FCSTD DOCUMENT  (FreeCAD 1.0R39109 (Git))
Label: Tail_Hinge_Inner
License: All rights reserved
LicenseURL: http://en.wikipedia.org/wiki/All_rights_reserved
objects: App::Link×3, Spreadsheet::Sheet×1, App::Part×1
EXTERNAL_REF file=Tail_Hinge_Inner_Pipe.FCStd obj=Tube
EXTERNAL_REF file=../../../Master_of_Puppets.FCStd obj=Spreadsheet
EXTERNAL_REF file=../../../Master_of_Puppets.FCStd obj=Tail
EXTERNAL_REF file=../Junction/Tail_Hinge_Junction.FCStd obj=Part
EXTERNAL_REF file=Tail_Hinge_Inner_Pipe_Cover.FCStd obj=Cylinder

FEATURE [App::Link] Link  label="Pipe"
  LinkPlacement = pos=(31.9025,0,-7.21663) rot=(0,1,0;0.349066rad)
  LinkedObject = -> <external Tail_Hinge_Inner_Pipe.FCStd>#Tube
  Placement = pos=(31.9025,0,-7.21663) rot=(0,1,0;0.349066rad)
  expr: .LinkPlacement.Base.x = Spreadsheet.TailHingePipeX
  expr: .LinkPlacement.Base.z = Spreadsheet.TailHingePipeZ
  expr: Placement = Spreadsheet.HingeInnerPipePlacement
FEATURE [Spreadsheet::Sheet] Spreadsheet
  cells = A1='Inputs; A2='VerticalPlaneAngle; B2(VerticalPlaneAngle)==Master_of_Puppets#Spreadsheet.VerticalPlaneAngle; A3='HingeInnerPipeRadius; B3(HingeInnerPipeRadius)==Master_of_Puppets#Tail.HingeInnerPipeRadius; A4='FlatMetalThickness; B4(FlatMetalThickness)==Master_of_Puppets#Spreadsheet.FlatMetalThickness; A5='Height; B5(Height)==Master_of_Puppets#Tail.TailHingeJunctionHeight; A6='Chamfer; B6(Chamfer)==Master_of_Puppets#Tail.TailHingeJunctionChamfer; A7='FullWidth; B7(FullWidth)==Master_of_Puppets#Tail.TailHingeJunctionFullWidth; A8='TailHingePipeZ; B8(TailHingePipeZ)==Master_of_Puppets#Tail.TailHingePipeZ; A9='TailHingePipeX; B9(TailHingePipeX)==Master_of_Puppets#Tail.TailHingePipeX; A10='HingeInnerPipeLength; B10(HingeInnerPipeLength)==Master_of_Puppets#Tail.HingeInnerPipeLength; A11='HingeInnerPipeDisplayCover; B11(HingeInnerPipeDisplayCover)==Master_of_Puppets#Tail.HingeInnerPipeDisplayCover; A12='Calculated; A13='TailHingeJunctionX; B13(TailHingeJunctionX)==-Chamfer; A14='HingeInnerPipePlacement; B14(HingeInnerPipePlacement)==placement(vector(TailHingePipeX; 0; TailHingePipeZ); vector(0; 1; 0); VerticalPlaneAngle); A15='HingeInnerPipeCoverPlacement; B15(HingeInnerPipeCoverPlacement)==HingeInnerPipePlacement * placement(vector(0; 0; HingeInnerPipeLength); vector(0; 0; 1); 0)
FEATURE [App::Link] Link005  label="Junction"
  LinkPlacement = pos=(-12.075,0,0) rot=(0,0,1;0rad)
  LinkedObject = -> <external ../Junction/Tail_Hinge_Junction.FCStd>#Part
  Placement = pos=(-12.075,0,0) rot=(0,0,1;0rad)
  expr: .Placement.Base.x = Spreadsheet.TailHingeJunctionX
FEATURE [App::Link] Link006  label="Tail_Hinge_Inner_Pipe_Cover"
  LinkPlacement = pos=(93.2691,0,161.387) rot=(0,1,0;0.349066rad)
  LinkedObject = -> <external Tail_Hinge_Inner_Pipe_Cover.FCStd>#Cylinder
  Placement = pos=(93.2691,0,161.387) rot=(0,1,0;0.349066rad)
  expr: Placement = Spreadsheet.HingeInnerPipeCoverPlacement
  expr: Visibility = Spreadsheet.HingeInnerPipeDisplayCover
FEATURE [App::Part] Part001  label="Tail_Hinge_Inner"
  Group = -> [Link,Link005,Link006]
  Origin = -> Origin001

RESOLVED EXTERNAL PARTS (link-assembly join: the EXTERNAL_REF files above that resolve inside this repo's crawl, each included once):
---- part ../../../Master_of_Puppets.FCStd = doc fcstd_6404554055c4 (61625 chars; too large to inline — full recipe in that document) ----
---- part ../Junction/Tail_Hinge_Junction.FCStd = doc fcstd_d0f173730f93 ----
FCSTD DOCUMENT  (FreeCAD 0.21R33675 (Git))
Label: Tail_Hinge_Junction
License: All rights reserved
LicenseURL: http://en.wikipedia.org/wiki/All_rights_reserved
objects: App::Link×3, Spreadsheet::Sheet×1, App::Part×1
EXTERNAL_REF file=../../../Master_of_Puppets.FCStd obj=Spreadsheet
EXTERNAL_REF file=../../../Master_of_Puppets.FCStd obj=Tail
EXTERNAL_REF file=Tail_Hinge_Junction_Cover_Top.FCStd obj=PocketBody
EXTERNAL_REF file=Tail_Hinge_Junction_Cover_Side.FCStd obj=PadBody

FEATURE [Spreadsheet::Sheet] Spreadsheet
  cells = A1='Inputs; A2='YawPipeDiameter; B2(YawPipeDiameter)==Master_of_Puppets#Spreadsheet.YawPipeDiameter; A3='HingeInnerPipeRadius; B3(HingeInnerPipeRadius)==Master_of_Puppets#Tail.HingeInnerPipeRadius; A4='FlatMetalThickness; B4(FlatMetalThickness)==Master_of_Puppets#Spreadsheet.FlatMetalThickness; A5='Height; B5(Height)==Master_of_Puppets#Tail.TailHingeJunctionHeight; A6='FullWidth; B6(FullWidth)==Master_of_Puppets#Tail.TailHingeJunctionFullWidth; A7='Calculated; A8='YawPipeRadius; B8(YawPipeRadius)==YawPipeDiameter / 2; A9='SideCoverAngle; B9(SideCoverAngle)==YawPipeRadius == HingeInnerPipeRadius ? 0 deg : 90 deg - atan(FullWidth / (YawPipeRadius - HingeInnerPipeRadius)); A10='TailHingeTopCoverZ; B10(TailHingeTopCoverZ)==Height - FlatMetalThickness; A11='FrontTailHingeSideCoverY; B11(FrontTailHingeSideCoverY)==-YawPipeRadius; A12='BackTailHingeSideCoverY; B12(BackTailHingeSideCoverY)==YawPipeRadius + FlatMetalThickness
FEATURE [App::Link] Link  label="Top_Cover"
  LinkPlacement = pos=(0,0,70) rot=(0,0,1;0rad)
  LinkedObject = -> <external Tail_Hinge_Junction_Cover_Top.FCStd>#PocketBody
  Placement = pos=(0,0,70) rot=(0,0,1;0rad)
  expr: .Placement.Base.z = Spreadsheet.TailHingeTopCoverZ
FEATURE [App::Link] Link001  label="Cover_Side_Front"
  LinkPlacement = pos=(0,-30.15,0) rot=(0,0,1;0rad)
  LinkTransform = true
  LinkedObject = -> <external Tail_Hinge_Junction_Cover_Side.FCStd>#PadBody
  Placement = pos=(0,-30.15,0) rot=(0,0,1;0rad)
  expr: .LinkPlacement.Base.y = Spreadsheet.FrontTailHingeSideCoverY
  expr: .LinkPlacement.Rotation.Angle = Spreadsheet.SideCoverAngle
FEATURE [App::Link] Link002  label="Cover_Side_Back"
  LinkPlacement = pos=(0,40.15,0) rot=(0,0,1;0rad)
  LinkTransform = true
  LinkedObject = -> <external Tail_Hinge_Junction_Cover_Side.FCStd>#PadBody
  Placement = pos=(0,40.15,0) rot=(0,0,1;0rad)
  expr: .LinkPlacement.Base.y = Spreadsheet.BackTailHingeSideCoverY
  expr: .LinkPlacement.Rotation.Angle = -Spreadsheet.SideCoverAngle
FEATURE [App::Part] Part  label="Tail_Hinge_Junction"
  Group = -> [Link,Link001,Link002]
  Origin = -> Origin
---- part Tail_Hinge_Inner_Pipe_Cover.FCStd = doc fcstd_27112a01b711 ----
FCSTD DOCUMENT  (FreeCAD 1.0R39109 (Git))
Label: Tail_Hinge_Inner_Pipe_Cover
Comment: Increasing the surface area of the inner tube with a cover helps prevent damage to the outer tube cover caused by friction and wear in larger turbines, especially for Star and larger H shapes.
License: All rights reserved
LicenseURL: http://en.wikipedia.org/wiki/All_rights_reserved
objects: Spreadsheet::Sheet×1, Part::Cylinder×1
note: 1 computed .brp shape members not serialized (recipe doc carries the construction recipe); baked Part::Feature solids carry a one-line shape summary decoded from their .brp
EXTERNAL_REF file=../../../Master_of_Puppets.FCStd obj=Spreadsheet
EXTERNAL_REF file=../../../Master_of_Puppets.FCStd obj=Tail

FEATURE [Spreadsheet::Sheet] Spreadsheet
  cells = A1='Inputs; A2='PipeThickness; B2(PipeThickness)==Master_of_Puppets#Spreadsheet.PipeThickness; A3='HingeInnerPipeCoverThickness; B3(HingeInnerPipeCoverThickness)==Master_of_Puppets#Tail.HingeInnerPipeCoverThickness; A4='HingeInnerPipeRadius; B4(HingeInnerPipeRadius)==Master_of_Puppets#Tail.HingeInnerPipeRadius; A5='Calculated; A6='HingeInnerPipeCoverRadius; B6(HingeInnerPipeCoverRadius)==HingeInnerPipeRadius - PipeThickness / 2
FEATURE [Part::Cylinder] Cylinder  label="Tail_Hinge_Inner_Pipe_Cover"
  Angle = 360
  AttacherType = Attacher::AttachEngine3D
  FirstAngle = 0
  Height = 5
  Openafpm_Flat = true
  Radius = 34
  SecondAngle = 0
  expr: Height = Spreadsheet.HingeInnerPipeCoverThickness
  expr: Radius = Spreadsheet.HingeInnerPipeCoverRadius
